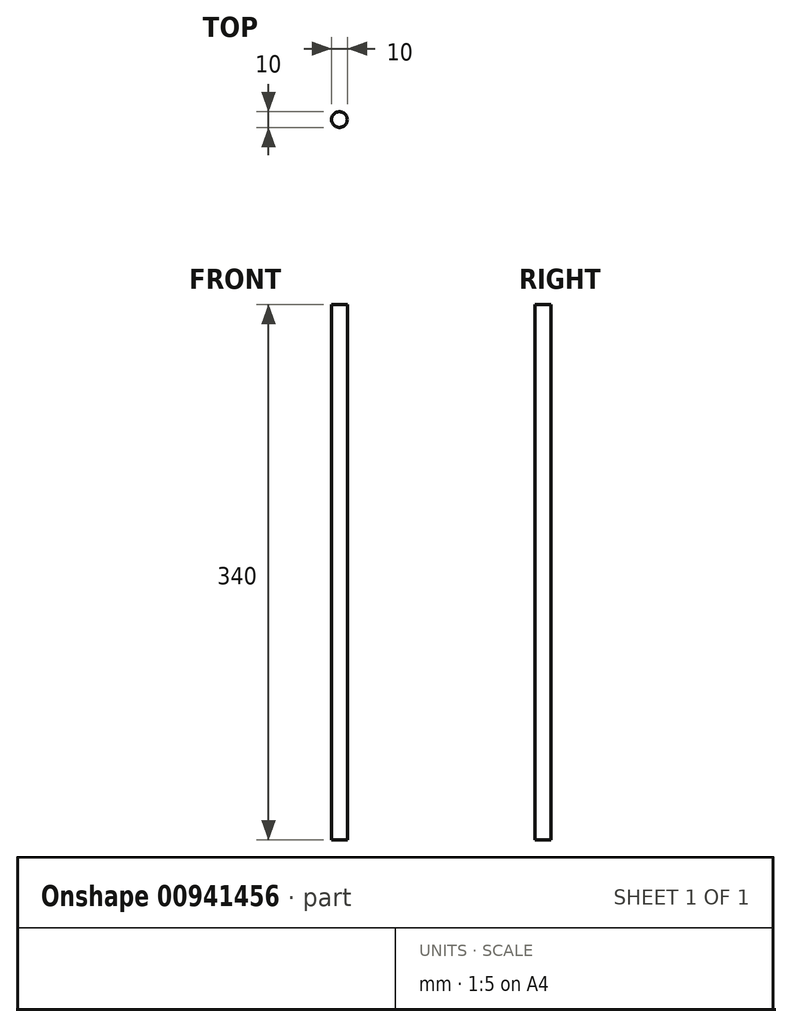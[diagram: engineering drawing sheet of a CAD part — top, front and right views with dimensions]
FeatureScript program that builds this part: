
annotation { "Feature Type Name" : "Feature", "Feature Type Description" : "" }
export const myFeature = defineFeature(function(context is Context, id is Id, definition is map)
    precondition{}
    {
        {
            var Q0;
            Q0=qCreatedBy(makeId("Top.planeOp"),FACE);
            var sketch = newSketch(context, id + "F0", { "sketchPlane" : qUnion([Q0])});
            skCircle(sketch, "E0", {"center": v(0, 0) * mm, "radius": 5 * mm});
            skSolve(sketch);
        }
        {
            var Q0;
            Q0=makeQuery(id+"F0.imprint","IMPRINT",FACE,{"disambiguationData":[TD([[makeQuery(id+"F0.imprint","IMPRINT",EDGE,{"derivedFrom":sQuery(id+"F0.wireOp",EDGE,"E0")}),1.0]])]});
            extrude(context, id + "F1", {"entities" : qUnion([Q0]), "depth" : 340 * mm, "offsetDistance" : 25 * mm});
        }
    });
